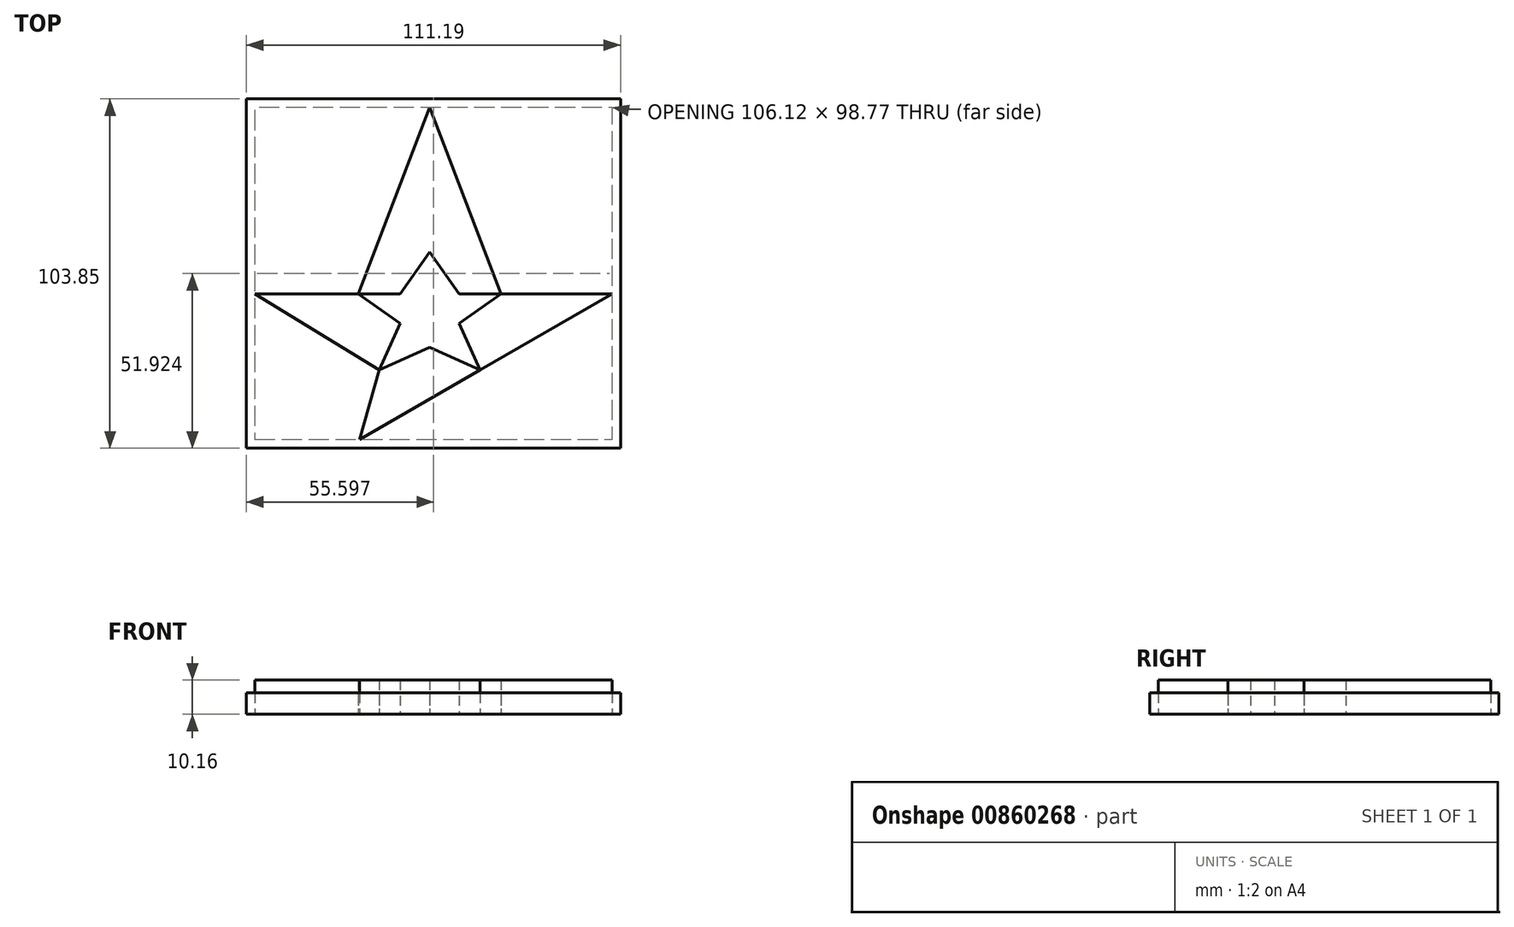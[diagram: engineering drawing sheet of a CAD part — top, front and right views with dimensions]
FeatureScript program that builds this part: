
annotation { "Feature Type Name" : "Feature", "Feature Type Description" : "" }
export const myFeature = defineFeature(function(context is Context, id is Id, definition is map)
    precondition{}
    {
        {
            var Q0;
            Q0=qCreatedBy(makeId("Top.planeOp"),FACE);
            var sketch = newSketch(context, id + "F0", { "sketchPlane" : qUnion([Q0])});
            skLineSegment(sketch, "E0", {"start": v(0, 12.48) * mm, "end": v(-8.74, 0) * mm});
            skLineSegment(sketch, "E1", {"start": v(-8.74, 0) * mm, "end": v(-21.23, 0) * mm});
            skLineSegment(sketch, "E2", {"start": v(-21.23, 0) * mm, "end": v(-8.74, -8.74) * mm});
            skLineSegment(sketch, "E3", {"start": v(-8.74, -8.74) * mm, "end": v(-14.98, -22.64) * mm});
            skPoint(sketch, "E3.endSnap0", {"position": v(-14.98, 0) * mm});
            skLineSegment(sketch, "E4", {"start": v(-14.98, -22.64) * mm, "end": v(0, -15.92) * mm});
            skLineSegment(sketch, "E5", {"start": v(0, 12.48) * mm, "end": v(8.74, 0) * mm});
            skLineSegment(sketch, "E6", {"start": v(8.74, 0) * mm, "end": v(21.23, 0) * mm});
            skLineSegment(sketch, "E7", {"start": v(21.23, 0) * mm, "end": v(8.74, -8.74) * mm});
            skLineSegment(sketch, "E8", {"start": v(8.74, -8.74) * mm, "end": v(14.98, -22.64) * mm});
            skLineSegment(sketch, "E9", {"start": v(14.98, -22.64) * mm, "end": v(0, -15.92) * mm});
            skLineSegment(sketch, "E10", {"start": v(-21.23, 0) * mm, "end": v(-51.91, 0) * mm});
            skLineSegment(sketch, "E11", {"start": v(21.23, 0) * mm, "end": v(54.2, 0) * mm});
            skLineSegment(sketch, "E12", {"start": v(-51.91, 0) * mm, "end": v(-14.98, -22.64) * mm});
            skLineSegment(sketch, "E13", {"start": v(54.2, 0) * mm, "end": v(-20.85, -43.33) * mm});
            skLineSegment(sketch, "E14", {"start": v(-20.85, -43.33) * mm, "end": v(-14.98, -22.64) * mm});
            skLineSegment(sketch, "E15", {"start": v(0, 55.44) * mm, "end": v(-21.23, 0) * mm});
            skLineSegment(sketch, "E16", {"start": v(0, 55.44) * mm, "end": v(21.23, 0) * mm});
            skLineSegment(sketch, "E17.bottom", {"start": v(-51.91, 57.98) * mm, "end": v(56.74, 57.98) * mm});
            skLineSegment(sketch, "E17.top", {"start": v(-51.91, -45.87) * mm, "end": v(56.74, -45.87) * mm});
            skLineSegment(sketch, "E17.right", {"start": v(56.74, 57.98) * mm, "end": v(56.74, -45.87) * mm});
            skLineSegment(sketch, "E18", {"start": v(-54.45, 57.98) * mm, "end": v(-54.45, -45.87) * mm});
            skLineSegment(sketch, "E19", {"start": v(-54.45, -45.87) * mm, "end": v(-51.91, -45.87) * mm});
            skLineSegment(sketch, "E20", {"start": v(-54.45, 57.98) * mm, "end": v(-51.91, 57.98) * mm});
            skSolve(sketch);
        }
        {
            var Q0;
            {var subQ0=sQuery(id+"F0.wireOp",EDGE,"E10");Q0=makeQuery(id+"F0.imprint","IMPRINT",FACE,{"disambiguationData":[TD([[makeQuery(id+"F0.imprint","IMPRINT",EDGE,{"derivedFrom":subQ0}),-1.0]])]});}
            var Q1;
            {var subQ0=sQuery(id+"F0.wireOp",EDGE,"E12");Q1=makeQuery(id+"F0.imprint","IMPRINT",FACE,{"disambiguationData":[TD([[makeQuery(id+"F0.imprint","IMPRINT",EDGE,{"derivedFrom":subQ0}),-1.0]])]});}
            var Q2;
            {var subQ2=sQuery(id+"F0.wireOp",EDGE,"nMXfX5id-fI1O-TMJ3-yFG7-MAwpaSaPuJWk.right");var subQ4=sQuery(id+"F0.wireOp",EDGE,"nMXfX5id-fI1O-TMJ3-yFG7-MAwpaSaPuJWk.top");var subQ6=makeQuery(id+"F0.imprint","INTERSECT",VERTEX,{"derivedFrom":[subQ4,subQ2]});Q2=makeQuery(id+"F0.imprint","IMPRINT",FACE,{"disambiguationData":[TD([[makeQuery(id+"F0.imprint","IMPRINT",EDGE,{"disambiguationData":[TD([[subQ6,1.0]])],"derivedFrom":subQ4}),1.0]])]});}
            var Q3;
            {var subQ0=sQuery(id+"F0.wireOp",EDGE,"E11");Q3=makeQuery(id+"F0.imprint","IMPRINT",FACE,{"disambiguationData":[TD([[makeQuery(id+"F0.imprint","IMPRINT",EDGE,{"derivedFrom":subQ0}),1.0]])]});}
            extrude(context, id + "F1", {"entities" : qUnion([Q0, Q1, Q2, Q3]), "depth" : 6.35 * mm, "offsetDistance" : 25.4 * mm});
        }
        {
            var Q0;
            Q0=makeQuery(id+"F0.imprint","IMPRINT",FACE,{"disambiguationData":[TD([[makeQuery(id+"F0.imprint","IMPRINT",EDGE,{"derivedFrom":sQuery(id+"F0.wireOp",EDGE,"E0")}),-1.0]])]});
            var Q1;
            Q1=makeQuery(id+"F0.imprint","IMPRINT",FACE,{"disambiguationData":[TD([[makeQuery(id+"F0.imprint","IMPRINT",EDGE,{"derivedFrom":sQuery(id+"F0.wireOp",EDGE,"E2")}),-1.0]])]});
            var Q2;
            Q2=makeQuery(id+"F0.imprint","IMPRINT",FACE,{"disambiguationData":[TD([[makeQuery(id+"F0.imprint","IMPRINT",EDGE,{"derivedFrom":sQuery(id+"F0.wireOp",EDGE,"E4")}),-1.0]])]});
            var Q3;
            Q3=makeQuery(id+"F0.imprint","IMPRINT",FACE,{"disambiguationData":[TD([[makeQuery(id+"F0.imprint","IMPRINT",EDGE,{"derivedFrom":sQuery(id+"F0.wireOp",EDGE,"E7")}),1.0]])]});
            extrude(context, id + "F2", {"entities" : qUnion([Q0, Q1, Q2, Q3]), "depth" : 10.16 * mm, "offsetDistance" : 25.4 * mm});
        }
    });
